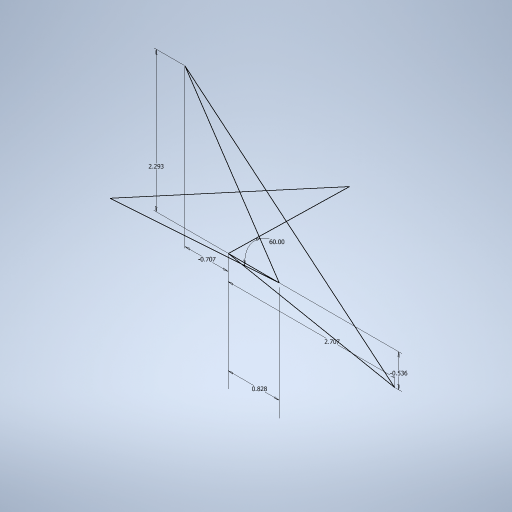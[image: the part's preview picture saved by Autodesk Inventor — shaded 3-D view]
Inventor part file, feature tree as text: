
AUTODESK INVENTOR PART (.ipt)
format: ipt  version: 2024 (Build 280153000, 153)  size: 241,152 bytes
history: native  units: in
note: dims shown in document units (in); Inventor stores cm internally (conversion verified against a paired STEP export)
features: sketch x1
ambient origin geometry x8: Origin, YZ Plane, XZ Plane, XY Plane, X Axis, Y Axis, Z Axis, Center Point
feature tree (1):
  sketch  "Sketch1"  dims[d0=0.0326in d1=-0.0278in d2=0.0903in d3=0.1066in d4=-0.0211in d5=-0.4123in]
